# Revit family: SOLCRAFTE_PLUS150-SO31462
name_source: partatom
category: Aparatos eléctricos
revit_build: Autodesk Revit 2016 (Build: 20150220_1215(x64)
units: mm (PartAtom-declared; Revit-internal decimal feet)

## family parameters
Compartido = No
Corte con vacíos al cargar = No
Cota de conector redondo = Diámetro de uso
Mantener orientación de anotación = No
Número OmniClass = 23.80.00.00
Punto de cálculo de habitación = No
Se basa en plano de trabajo = No
Siempre vertical = Sí
Tipo de pieza = Caja de conexiones
Título OmniClass = Electric Power and Lighting

## types (1)
- SOLCRAFTE PLUS 150
    Aislamiento = 30 mm espuma PU
    Altura = 212 mm
    Anchura = 800 mm
    Capacidad = 145 l
    Certificación ministerio = SS-15513
    Conexiones = 2 x3/4" conexiones macho
    Costo = 0 $
    Código de montaje = SO31462
    Descripción = CAPTADOR SOLAR CON ACUMULADOR
    Fabricante = SALVADOR ESCODA
    Imagen de tipo = Solcrafte_Plus.jpg
    Instalación = cubierta plana / cubierta inclinada
    Longitud = 2184 mm
    Modelo = SOLCRAFTE PLUS 150L
    Peso (vacio, sin elem. fij.) = 60 Kg
    Pres. máx. de trabajo = 4 bar
    Resistencia elec. opcional = 1 kW
    Superfície total captador = 1.75 m2
    Temp. máx. trabajo = 95 ºC
    URL = www.salvadorescoda.com
